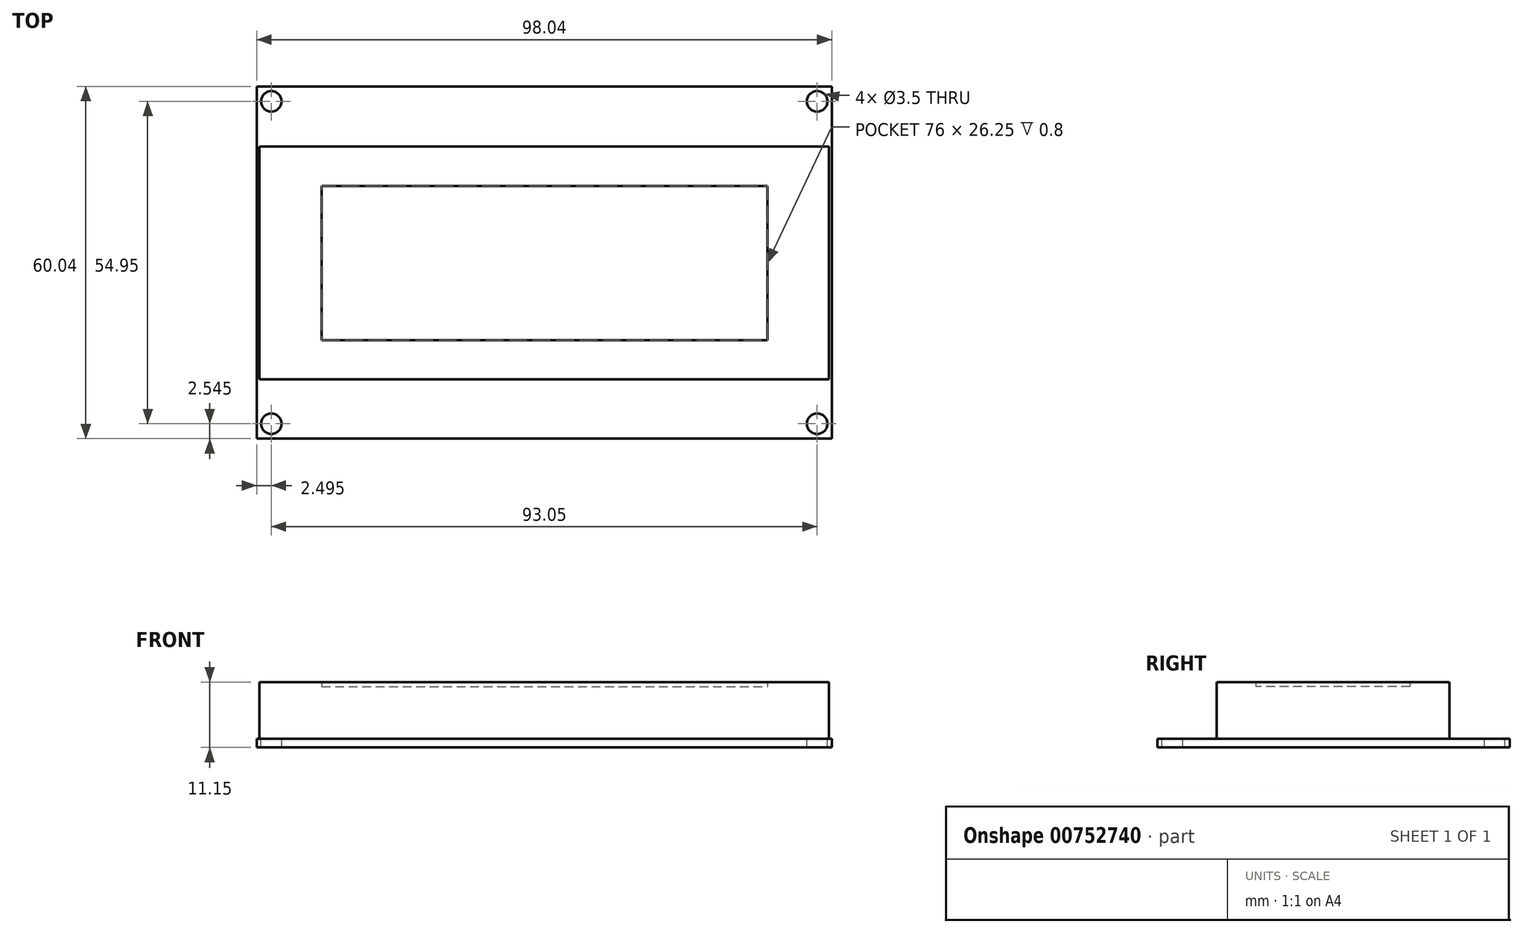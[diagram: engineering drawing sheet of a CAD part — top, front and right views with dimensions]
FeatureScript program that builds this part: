
annotation { "Feature Type Name" : "Feature", "Feature Type Description" : "" }
export const myFeature = defineFeature(function(context is Context, id is Id, definition is map)
    precondition{}
    {
        {
            var Q0;
            Q0=qCreatedBy(makeId("Top.planeOp"),FACE);
            var sketch = newSketch(context, id + "F0", { "sketchPlane" : qUnion([Q0])});
            skLineSegment(sketch, "E0.bottom", {"start": v(-49.02, 30.02) * mm, "end": v(49.02, 30.02) * mm});
            skLineSegment(sketch, "E0.top", {"start": v(-49.02, -30.02) * mm, "end": v(49.03, -30.02) * mm});
            skLineSegment(sketch, "E0.left", {"start": v(-49.02, 30.02) * mm, "end": v(-49.02, -30.02) * mm});
            skLineSegment(sketch, "E0.right", {"start": v(49.02, 30.03) * mm, "end": v(49.02, -30.02) * mm});
            skLineSegment(sketch, "E1.bottom", {"start": v(-48.52, 19.78) * mm, "end": v(48.52, 19.78) * mm});
            skLineSegment(sketch, "E1.top", {"start": v(-48.52, -19.92) * mm, "end": v(48.53, -19.92) * mm});
            skLineSegment(sketch, "E1.left", {"start": v(-48.53, 19.78) * mm, "end": v(-48.53, -19.92) * mm});
            skLineSegment(sketch, "E1.right", {"start": v(48.52, 19.78) * mm, "end": v(48.52, -19.92) * mm});
            skCircle(sketch, "E2", {"center": v(-46.53, 27.48) * mm, "radius": 1.75 * mm});
            skCircle(sketch, "E3.MirrorC", {"center": v(-46.53, -27.48) * mm, "radius": 1.75 * mm});
            skCircle(sketch, "E4.MirrorC", {"center": v(46.53, 27.48) * mm, "radius": 1.75 * mm});
            skCircle(sketch, "E5.MirrorC", {"center": v(46.53, -27.48) * mm, "radius": 1.75 * mm});
            skLineSegment(sketch, "E6", {"start": v(0, 0) * mm, "end": v(0, 30.02) * mm, "construction": true});
            skLineSegment(sketch, "E7.bottom", {"start": v(-37.92, 13.02) * mm, "end": v(38.08, 13.02) * mm});
            skLineSegment(sketch, "E7.top", {"start": v(-37.92, -13.23) * mm, "end": v(38.08, -13.23) * mm});
            skLineSegment(sketch, "E7.left", {"start": v(-37.92, 13.02) * mm, "end": v(-37.92, -13.23) * mm});
            skLineSegment(sketch, "E7.right", {"start": v(38.07, 13.02) * mm, "end": v(38.07, -13.23) * mm});
            skLineSegment(sketch, "E8.bottom", {"start": v(-45, 17) * mm, "end": v(45, 17) * mm});
            skLineSegment(sketch, "E8.top", {"start": v(-45, -17) * mm, "end": v(45, -17) * mm});
            skLineSegment(sketch, "E8.left", {"start": v(-45, 17) * mm, "end": v(-45, -17) * mm});
            skLineSegment(sketch, "E8.right", {"start": v(45, 17) * mm, "end": v(45, -17) * mm});
            skLineSegment(sketch, "E9", {"start": v(0, 0) * mm, "end": v(0, -17) * mm, "construction": true});
            skSolve(sketch);
        }
        {
            var Q0;
            Q0=makeQuery(id+"F0.imprint","IMPRINT",FACE,{"disambiguationData":[TD([[makeQuery(id+"F0.imprint","IMPRINT",EDGE,{"derivedFrom":sQuery(id+"F0.wireOp",EDGE,"E0.bottom")}),-1.0]])]});
            var Q1;
            Q1=makeQuery(id+"F0.imprint","IMPRINT",FACE,{"disambiguationData":[TD([[makeQuery(id+"F0.imprint","IMPRINT",EDGE,{"derivedFrom":sQuery(id+"F0.wireOp",EDGE,"E7.bottom")}),-1.0]])]});
            var Q2;
            Q2=makeQuery(id+"F0.imprint","IMPRINT",FACE,{"disambiguationData":[TD([[makeQuery(id+"F0.imprint","IMPRINT",EDGE,{"derivedFrom":sQuery(id+"F0.wireOp",EDGE,"E7.bottom")}),1.0]])]});
            var Q3;
            Q3=makeQuery(id+"F0.imprint","IMPRINT",FACE,{"disambiguationData":[TD([[makeQuery(id+"F0.imprint","IMPRINT",EDGE,{"derivedFrom":sQuery(id+"F0.wireOp",EDGE,"E1.bottom")}),-1.0]])]});
            extrude(context, id + "F1", {"entities" : qUnion([Q0, Q1, Q2, Q3]), "depth" : -1.5 * mm, "offsetDistance" : 25 * mm});
        }
        {
            var Q0;
            Q0=makeQuery(id+"F0.imprint","IMPRINT",FACE,{"disambiguationData":[TD([[makeQuery(id+"F0.imprint","IMPRINT",EDGE,{"derivedFrom":sQuery(id+"F0.wireOp",EDGE,"E1.bottom")}),-1.0]])]});
            var Q1;
            Q1=makeQuery(id+"F0.imprint","IMPRINT",FACE,{"disambiguationData":[TD([[makeQuery(id+"F0.imprint","IMPRINT",EDGE,{"derivedFrom":sQuery(id+"F0.wireOp",EDGE,"E7.bottom")}),1.0]])]});
            extrude(context, id + "F2", {"entities" : qUnion([Q0, Q1]), "operationType" : NewBodyOperationType.ADD, "depth" : 9.65 * mm, "offsetDistance" : 25 * mm});
        }
        {
            var Q0;
            Q0=makeQuery(id+"F0.imprint","IMPRINT",FACE,{"disambiguationData":[TD([[makeQuery(id+"F0.imprint","IMPRINT",EDGE,{"derivedFrom":sQuery(id+"F0.wireOp",EDGE,"E7.bottom")}),-1.0]])]});
            extrude(context, id + "F3", {"entities" : qUnion([Q0]), "operationType" : NewBodyOperationType.ADD, "depth" : 8.85 * mm, "offsetDistance" : 25 * mm});
        }
    });
